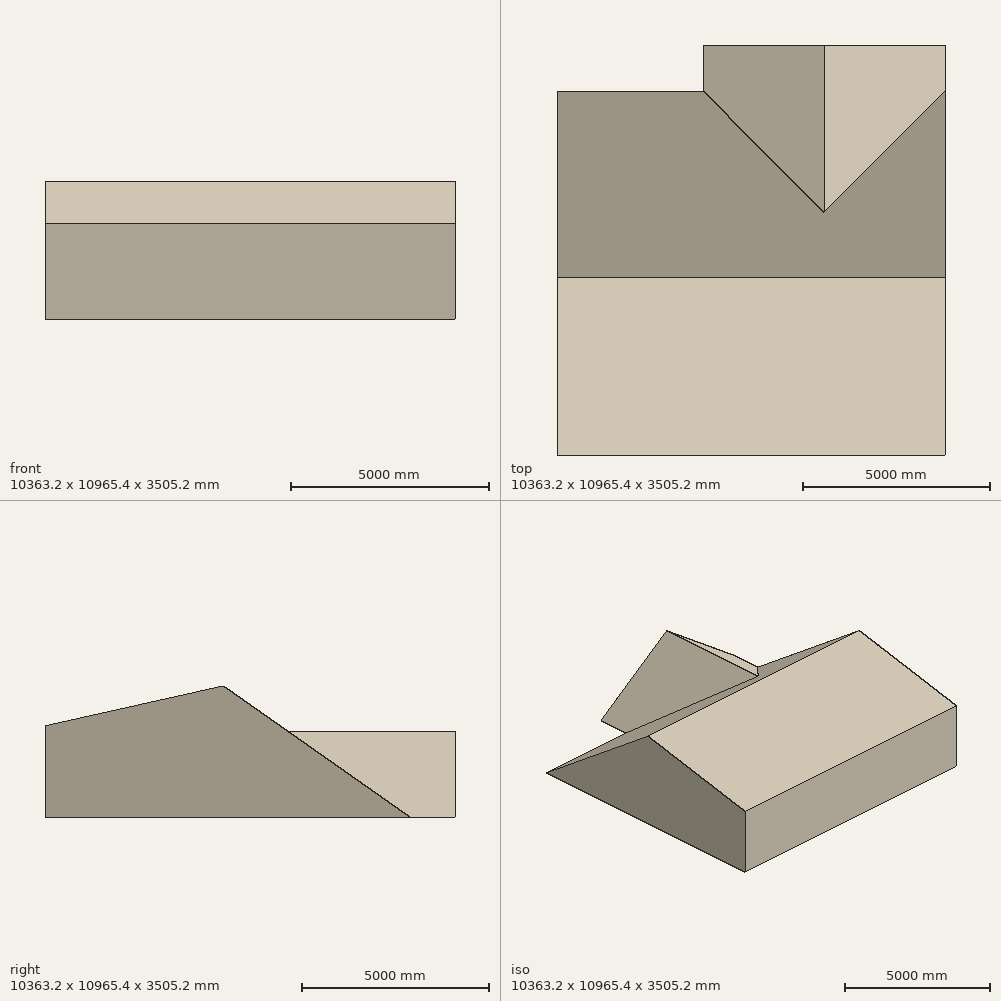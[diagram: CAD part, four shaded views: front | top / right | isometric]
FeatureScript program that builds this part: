
annotation { "Feature Type Name" : "Feature", "Feature Type Description" : "" }
export const myFeature = defineFeature(function(context is Context, id is Id, definition is map)
    precondition{}
    {
        {
            var Q0;
            Q0=qCreatedBy(makeId("Right.planeOp"),FACE);
            var sketch = newSketch(context, id + "F0", { "sketchPlane" : qUnion([Q0])});
            skLineSegment(sketch, "E0", {"start": v(0, 0) * mm, "end": v(9746.15, 0) * mm});
            skLineSegment(sketch, "E1", {"start": v(9746.15, 0) * mm, "end": v(4758.69, 3505.2) * mm});
            skLineSegment(sketch, "E2", {"start": v(4758.69, 3505.2) * mm, "end": v(0, 2438.4) * mm});
            skLineSegment(sketch, "E3", {"start": v(0, 2438.4) * mm, "end": v(0, 0) * mm});
            skSolve(sketch);
        }
        {
            var Q0;
            Q0 = qSketchRegion(id + "F0", true);
            extrude(context, id + "F1", {"entities" : qUnion([Q0]), "depth" : 10363.2 * mm});
        }
        {
            var Q0;
            Q0=makeQuery(id+"F1.opExtrude","SWEPT_EDGE",EDGE,{"disambiguationData":[OSD([sQuery(id+"F0.wireOp",EDGE,"E0"),sQuery(id+"F0.wireOp",EDGE,"E1")])]});
            cPlane(context, id + "F2", {"entities" : qUnion([Q0]), "cplaneType" : CPlaneType.LINE_ANGLE, "offset" : 25.4 * mm, "angle" : 0 * degree, "width" : 152.4 * mm, "height" : 152.4 * mm});
        }
        {
            var Q0;
            Q0=qCreatedBy(id+"F2.planeOp",FACE);
            cPlane(context, id + "F3", {"entities" : qUnion([Q0]), "cplaneType" : CPlaneType.OFFSET, "offset" : 1219.2 * mm, "oppositeDirection" : true, "width" : 152.4 * mm, "height" : 152.4 * mm});
        }
        {
            var Q0;
            Q0=qCreatedBy(id+"F3.planeOp",FACE);
            var sketch = newSketch(context, id + "F4", { "sketchPlane" : qUnion([Q0])});
            skLineSegment(sketch, "E4", {"start": v(10363.2, 0) * mm, "end": v(7126.72, 2286) * mm});
            skLineSegment(sketch, "E5", {"start": v(7126.72, 2286) * mm, "end": v(3890.24, 0) * mm});
            skLineSegment(sketch, "E6", {"start": v(10363.2, 0) * mm, "end": v(3890.24, 0) * mm});
            skSolve(sketch);
        }
        {
            var Q0;
            Q0=makeQuery(id+"F4.imprint","IMPRINT",FACE,{"disambiguationData":[TD([[makeQuery(id+"F4.imprint","IMPRINT",EDGE,{"derivedFrom":sQuery(id+"F4.wireOp",EDGE,"E4")}),1.0]])]});
            extrude(context, id + "F5", {"entities" : qUnion([Q0]), "operationType" : NewBodyOperationType.ADD, "depth" : 4572 * mm});
        }
    });
